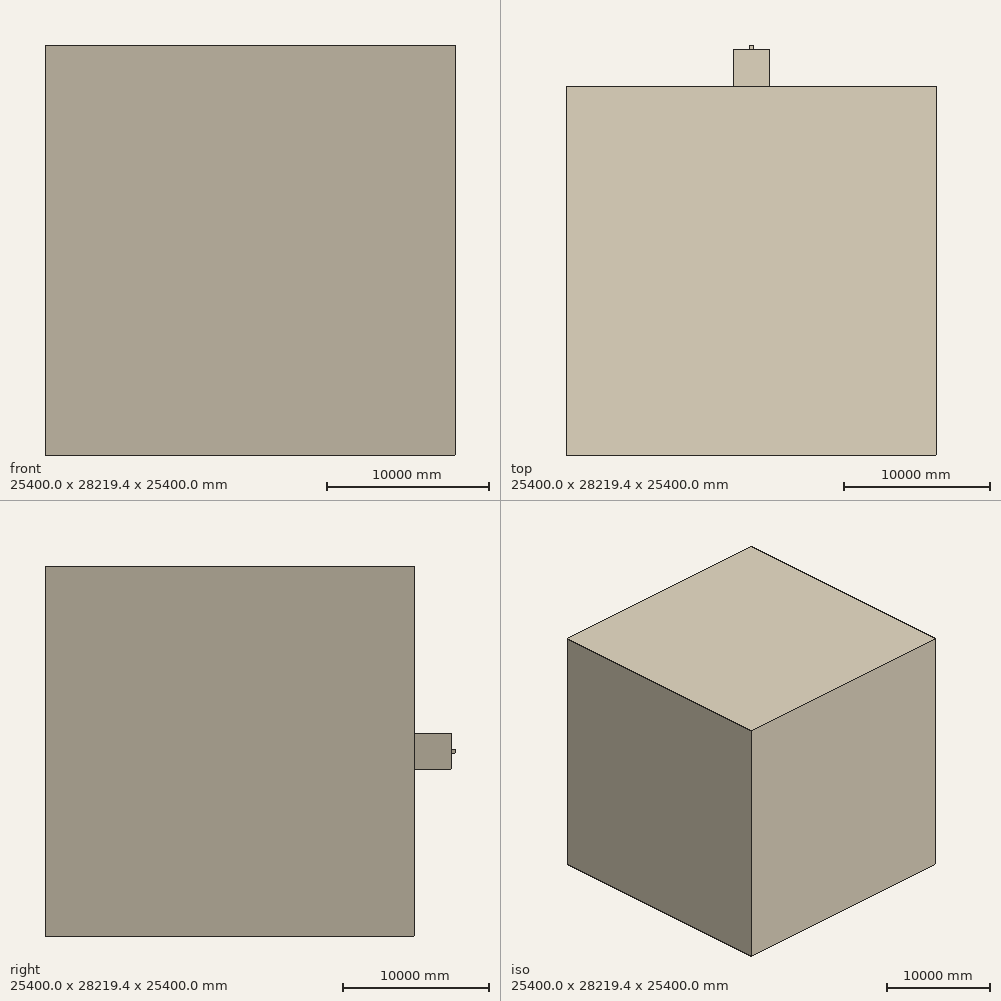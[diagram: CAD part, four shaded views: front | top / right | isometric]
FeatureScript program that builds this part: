
annotation { "Feature Type Name" : "Feature", "Feature Type Description" : "" }
export const myFeature = defineFeature(function(context is Context, id is Id, definition is map)
    precondition{}
    {
        {
            var Q0;
            Q0=qCreatedBy(makeId("Front.planeOp"),FACE);
            var sketch = newSketch(context, id + "F0", { "sketchPlane" : qUnion([Q0])});
            skLineSegment(sketch, "E0", {"start": v(0, 0) * mm, "end": v(25.4, 0) * mm});
            skLineSegment(sketch, "E1", {"start": v(0, 0) * mm, "end": v(0, 25.4) * mm});
            skLineSegment(sketch, "E2.bottom", {"start": v(127, -127) * mm, "end": v(-127, -127) * mm});
            skLineSegment(sketch, "E2.top", {"start": v(127, 127) * mm, "end": v(-127, 127) * mm});
            skLineSegment(sketch, "E2.left", {"start": v(127, -127) * mm, "end": v(127, 127) * mm});
            skLineSegment(sketch, "E2.right", {"start": v(-127, -127) * mm, "end": v(-127, 127) * mm});
            skPoint(sketch, "E2.middle", {"position": v(0, 0) * mm});
            skSolve(sketch);
        }
        {
            var Q0;
            Q0 = qSketchRegion(id + "F0", true);
            extrude(context, id + "F1", {"entities" : qUnion([Q0]), "endBound" : BoundingType.SYMMETRIC, "depth" : 254 * mm});
        }
        {
            var Q0;
            Q0=makeQuery(id+"F1.opExtrude","CAP_FACE",FACE,{"disambiguationData":[OSD([sQuery(id+"F0.wireOp",EDGE,"E2.bottom"),sQuery(id+"F0.wireOp",EDGE,"E2.top"),sQuery(id+"F0.wireOp",EDGE,"E2.left"),sQuery(id+"F0.wireOp",EDGE,"E2.right")])],"isStart":false});
            var sketch = newSketch(context, id + "F2", { "sketchPlane" : qUnion([Q0])});
            skLineSegment(sketch, "E3.bottom", {"start": v(1270, 1270) * mm, "end": v(-1270, 1270) * mm});
            skLineSegment(sketch, "E3.top", {"start": v(1270, -1270) * mm, "end": v(-1270, -1270) * mm});
            skLineSegment(sketch, "E3.left", {"start": v(1270, 1270) * mm, "end": v(1270, -1270) * mm});
            skLineSegment(sketch, "E3.right", {"start": v(-1270, 1270) * mm, "end": v(-1270, -1270) * mm});
            skPoint(sketch, "E3.middle", {"position": v(0, 0) * mm});
            skSolve(sketch);
        }
        {
            var Q0;
            Q0 = qSketchRegion(id + "F2", true);
            extrude(context, id + "F3", {"entities" : qUnion([Q0]), "operationType" : NewBodyOperationType.ADD, "depth" : 2540 * mm});
        }
        {
            var Q0;
            Q0=makeQuery(id+"F1.opExtrude","CAP_FACE",FACE,{"disambiguationData":[OSD([sQuery(id+"F0.wireOp",EDGE,"E2.bottom"),sQuery(id+"F0.wireOp",EDGE,"E2.top"),sQuery(id+"F0.wireOp",EDGE,"E2.left"),sQuery(id+"F0.wireOp",EDGE,"E2.right")])],"isStart":true});
            var sketch = newSketch(context, id + "F4", { "sketchPlane" : qUnion([Q0])});
            skLineSegment(sketch, "E4.bottom", {"start": v(12.7, -12.7) * mm, "end": v(-12.7, -12.7) * mm});
            skLineSegment(sketch, "E4.top", {"start": v(12.7, 12.7) * mm, "end": v(-12.7, 12.7) * mm});
            skLineSegment(sketch, "E4.left", {"start": v(12.7, -12.7) * mm, "end": v(12.7, 12.7) * mm});
            skLineSegment(sketch, "E4.right", {"start": v(-12.7, -12.7) * mm, "end": v(-12.7, 12.7) * mm});
            skPoint(sketch, "E4.middle", {"position": v(0, 0) * mm});
            skSolve(sketch);
        }
        {
            var Q0;
            Q0 = qSketchRegion(id + "F4", true);
            extrude(context, id + "F5", {"entities" : qUnion([Q0]), "operationType" : NewBodyOperationType.ADD, "depth" : 25.4 * mm});
        }
        {
            var Q0;
            Q0=makeQuery(id+"F3.opExtrude","CAP_FACE",FACE,{"disambiguationData":[OSD([sQuery(id+"F2.wireOp",EDGE,"E3.bottom"),sQuery(id+"F2.wireOp",EDGE,"E3.top"),sQuery(id+"F2.wireOp",EDGE,"E3.left"),sQuery(id+"F2.wireOp",EDGE,"E3.right")])],"isStart":false});
            var sketch = newSketch(context, id + "F6", { "sketchPlane" : qUnion([Q0])});
            skLineSegment(sketch, "E5.bottom", {"start": v(-12700, -12700) * mm, "end": v(12700, -12700) * mm});
            skLineSegment(sketch, "E5.top", {"start": v(-12700, 12700) * mm, "end": v(12700, 12700) * mm});
            skLineSegment(sketch, "E5.left", {"start": v(-12700, -12700) * mm, "end": v(-12700, 12700) * mm});
            skLineSegment(sketch, "E5.right", {"start": v(12700, -12700) * mm, "end": v(12700, 12700) * mm});
            skPoint(sketch, "E5.middle", {"position": v(0, 0) * mm});
            skSolve(sketch);
        }
        {
            var Q0;
            Q0 = qSketchRegion(id + "F6", true);
            extrude(context, id + "F7", {"entities" : qUnion([Q0]), "operationType" : NewBodyOperationType.ADD, "depth" : 25400 * mm});
        }
    });
